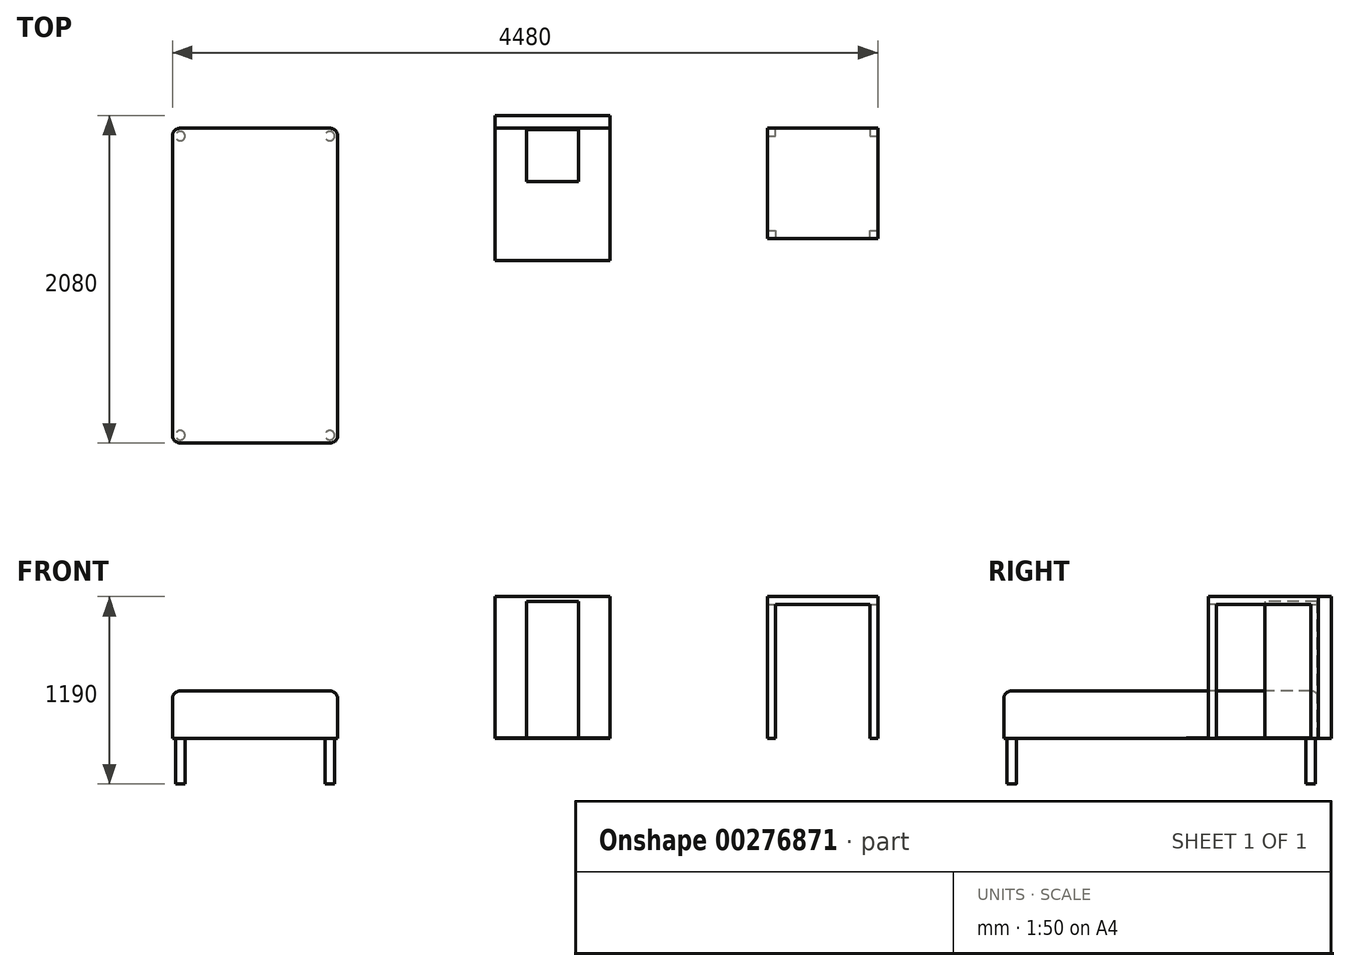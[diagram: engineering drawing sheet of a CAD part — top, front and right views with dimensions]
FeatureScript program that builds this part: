
annotation { "Feature Type Name" : "Feature", "Feature Type Description" : "" }
export const myFeature = defineFeature(function(context is Context, id is Id, definition is map)
    precondition{}
    {
        {
            var Q0;
            Q0=qCreatedBy(makeId("Top.planeOp"),FACE);
            var sketch = newSketch(context, id + "F0", { "sketchPlane" : qUnion([Q0])});
            skLineSegment(sketch, "E0.bottom", {"start": v(-500, 0) * mm, "end": v(-1550, 0) * mm});
            skLineSegment(sketch, "E0.top", {"start": v(-500, -2000) * mm, "end": v(-1550, -2000) * mm});
            skLineSegment(sketch, "E0.left", {"start": v(-500, 0) * mm, "end": v(-500, -2000) * mm});
            skLineSegment(sketch, "E0.right", {"start": v(-1550, 0) * mm, "end": v(-1550, -2000) * mm});
            skCircle(sketch, "E1", {"center": v(-1500, -50) * mm, "radius": 30 * mm});
            skCircle(sketch, "E2", {"center": v(-550, -50) * mm, "radius": 30 * mm});
            skCircle(sketch, "E3", {"center": v(-1500, -1950) * mm, "radius": 30 * mm});
            skCircle(sketch, "E4", {"center": v(-550, -1950) * mm, "radius": 30 * mm});
            skLineSegment(sketch, "E5.bottom", {"start": v(500, 0) * mm, "end": v(1230, 0) * mm});
            skLineSegment(sketch, "E5.top", {"start": v(500, -840) * mm, "end": v(1230, -840) * mm});
            skLineSegment(sketch, "E5.left", {"start": v(500, 0) * mm, "end": v(500, -840) * mm});
            skLineSegment(sketch, "E5.right", {"start": v(1230, 0) * mm, "end": v(1230, -840) * mm});
            skLineSegment(sketch, "E6.bottom", {"start": v(700, -10) * mm, "end": v(1030, -10) * mm});
            skLineSegment(sketch, "E6.top", {"start": v(700, -340) * mm, "end": v(1030, -340) * mm});
            skLineSegment(sketch, "E6.left", {"start": v(700, -10) * mm, "end": v(700, -340) * mm});
            skLineSegment(sketch, "E6.right", {"start": v(1030, -10) * mm, "end": v(1030, -340) * mm});
            skLineSegment(sketch, "E7", {"start": v(500, 0) * mm, "end": v(500, 80) * mm});
            skLineSegment(sketch, "E8", {"start": v(500, 80) * mm, "end": v(1230, 80) * mm});
            skLineSegment(sketch, "E9", {"start": v(1230, 80) * mm, "end": v(1230, 0) * mm});
            skSolve(sketch);
        }
        {
            var Q0;
            Q0=makeQuery(id+"F0.imprint","IMPRINT",FACE,{"disambiguationData":[TD([[makeQuery(id+"F0.imprint","IMPRINT",EDGE,{"derivedFrom":sQuery(id+"F0.wireOp",EDGE,"E0.bottom")}),1.0]])]});
            var Q1;
            Q1=makeQuery(id+"F0.imprint","IMPRINT",FACE,{"disambiguationData":[TD([[makeQuery(id+"F0.imprint","IMPRINT",EDGE,{"derivedFrom":sQuery(id+"F0.wireOp",EDGE,"E1")}),1.0]])]});
            var Q2;
            Q2=makeQuery(id+"F0.imprint","IMPRINT",FACE,{"disambiguationData":[TD([[makeQuery(id+"F0.imprint","IMPRINT",EDGE,{"derivedFrom":sQuery(id+"F0.wireOp",EDGE,"E2")}),1.0]])]});
            var Q3;
            Q3=makeQuery(id+"F0.imprint","IMPRINT",FACE,{"disambiguationData":[TD([[makeQuery(id+"F0.imprint","IMPRINT",EDGE,{"derivedFrom":sQuery(id+"F0.wireOp",EDGE,"E4")}),1.0]])]});
            var Q4;
            Q4=makeQuery(id+"F0.imprint","IMPRINT",FACE,{"disambiguationData":[TD([[makeQuery(id+"F0.imprint","IMPRINT",EDGE,{"derivedFrom":sQuery(id+"F0.wireOp",EDGE,"E3")}),1.0]])]});
            extrude(context, id + "F1", {"entities" : qUnion([Q0, Q1, Q2, Q3, Q4]), "depth" : 300 * mm});
        }
        {
            var Q0;
            Q0=makeQuery(id+"F0.imprint","IMPRINT",FACE,{"disambiguationData":[TD([[makeQuery(id+"F0.imprint","IMPRINT",EDGE,{"derivedFrom":sQuery(id+"F0.wireOp",EDGE,"E2")}),1.0]])]});
            var Q1;
            Q1=makeQuery(id+"F0.imprint","IMPRINT",FACE,{"disambiguationData":[TD([[makeQuery(id+"F0.imprint","IMPRINT",EDGE,{"derivedFrom":sQuery(id+"F0.wireOp",EDGE,"E1")}),1.0]])]});
            var Q2;
            Q2=makeQuery(id+"F0.imprint","IMPRINT",FACE,{"disambiguationData":[TD([[makeQuery(id+"F0.imprint","IMPRINT",EDGE,{"derivedFrom":sQuery(id+"F0.wireOp",EDGE,"E3")}),1.0]])]});
            var Q3;
            Q3=makeQuery(id+"F0.imprint","IMPRINT",FACE,{"disambiguationData":[TD([[makeQuery(id+"F0.imprint","IMPRINT",EDGE,{"derivedFrom":sQuery(id+"F0.wireOp",EDGE,"E4")}),1.0]])]});
            extrude(context, id + "F2", {"entities" : qUnion([Q0, Q1, Q2, Q3]), "operationType" : NewBodyOperationType.ADD, "oppositeDirection" : true, "depth" : 290 * mm});
        }
        {
            var Q0;
            Q0=makeQuery(id+"F1.opExtrude","SWEPT_EDGE",EDGE,{"disambiguationData":[OSD([sQuery(id+"F0.wireOp",EDGE,"E0.bottom"),sQuery(id+"F0.wireOp",EDGE,"E0.right")])]});
            var Q1;
            Q1=makeQuery(id+"F1.opExtrude","SWEPT_EDGE",EDGE,{"disambiguationData":[OSD([sQuery(id+"F0.wireOp",EDGE,"E0.top"),sQuery(id+"F0.wireOp",EDGE,"E0.right")])]});
            var Q2;
            Q2=makeQuery(id+"F1.opExtrude","SWEPT_EDGE",EDGE,{"disambiguationData":[OSD([sQuery(id+"F0.wireOp",EDGE,"E0.top"),sQuery(id+"F0.wireOp",EDGE,"E0.left")])]});
            var Q3;
            Q3=makeQuery(id+"F1.opExtrude","SWEPT_EDGE",EDGE,{"disambiguationData":[OSD([sQuery(id+"F0.wireOp",EDGE,"E0.bottom"),sQuery(id+"F0.wireOp",EDGE,"E0.left")])]});
            var Q4;
            Q4=makeQuery(id+"F1.opExtrude","CAP_FACE",FACE,{"disambiguationData":[OSD([sQuery(id+"F0.wireOp",EDGE,"E0.bottom"),sQuery(id+"F0.wireOp",EDGE,"E0.top"),sQuery(id+"F0.wireOp",EDGE,"E0.left"),sQuery(id+"F0.wireOp",EDGE,"E0.right")])],"isStart":false});
            fillet(context, id + "F3", {"entities" : qUnion([Q0, Q1, Q2, Q3, Q4]), "radius" : 50 * mm, "tangentPropagation" : true, "allowEdgeOverflow" : false});
        }
        {
            var Q0;
            Q0=makeQuery(id+"F0.imprint","IMPRINT",FACE,{"disambiguationData":[TD([[makeQuery(id+"F0.imprint","IMPRINT",EDGE,{"derivedFrom":sQuery(id+"F0.wireOp",EDGE,"E6.bottom")}),-1.0]])]});
            extrude(context, id + "F4", {"entities" : qUnion([Q0]), "depth" : 870 * mm});
        }
        {
            var Q0;
            Q0=makeQuery(id+"F0.imprint","IMPRINT",FACE,{"disambiguationData":[TD([[makeQuery(id+"F0.imprint","IMPRINT",EDGE,{"derivedFrom":sQuery(id+"F0.wireOp",EDGE,"E5.bottom")}),-1.0]])]});
            extrude(context, id + "F5", {"entities" : qUnion([Q0]), "operationType" : NewBodyOperationType.ADD, "depth" : 2 * mm});
        }
        {
            var Q0;
            Q0=makeQuery(id+"F0.imprint","IMPRINT",FACE,{"disambiguationData":[TD([[makeQuery(id+"F0.imprint","IMPRINT",EDGE,{"derivedFrom":sQuery(id+"F0.wireOp",EDGE,"E5.bottom")}),1.0]])]});
            extrude(context, id + "F6", {"entities" : qUnion([Q0]), "operationType" : NewBodyOperationType.ADD, "depth" : 900 * mm});
        }
        {
            var Q0;
            Q0=qCreatedBy(makeId("Top.planeOp"),FACE);
            cPlane(context, id + "F7", {"entities" : qUnion([Q0]), "cplaneType" : CPlaneType.OFFSET, "offset" : 900 * mm, "width" : 150 * mm, "height" : 150 * mm});
        }
        {
            var Q0;
            Q0=qCreatedBy(id+"F7.planeOp",FACE);
            var sketch = newSketch(context, id + "F8", { "sketchPlane" : qUnion([Q0])});
            skLineSegment(sketch, "E10.bottom", {"start": v(2230, 0) * mm, "end": v(2930, 0) * mm});
            skLineSegment(sketch, "E10.top", {"start": v(2230, -700) * mm, "end": v(2930, -700) * mm});
            skLineSegment(sketch, "E10.left", {"start": v(2230, 0) * mm, "end": v(2230, -700) * mm});
            skLineSegment(sketch, "E10.right", {"start": v(2930, 0) * mm, "end": v(2930, -700) * mm});
            skLineSegment(sketch, "E11", {"start": v(2230, -650) * mm, "end": v(2280, -650) * mm});
            skLineSegment(sketch, "E12", {"start": v(2280, -650) * mm, "end": v(2280, -700) * mm});
            skLineSegment(sketch, "E13", {"start": v(2880, 0) * mm, "end": v(2880, -50) * mm});
            skLineSegment(sketch, "E14", {"start": v(2880, -50) * mm, "end": v(2930, -50) * mm});
            skLineSegment(sketch, "E15", {"start": v(2230, -50) * mm, "end": v(2280, -50) * mm});
            skLineSegment(sketch, "E16", {"start": v(2280, -50) * mm, "end": v(2280, 0) * mm});
            skLineSegment(sketch, "E17", {"start": v(2880, -700) * mm, "end": v(2880, -650) * mm});
            skLineSegment(sketch, "E18", {"start": v(2880, -650) * mm, "end": v(2930, -650) * mm});
            skSolve(sketch);
        }
        {
            var Q0;
            {var subQ4=sQuery(id+"F8.wireOp",EDGE,"E11");Q0=makeQuery(id+"F8.imprint","IMPRINT",FACE,{"disambiguationData":[TD([[makeQuery(id+"F8.imprint","IMPRINT",EDGE,{"derivedFrom":subQ4}),1.0]])]});}
            var Q1;
            {var subQ4=sQuery(id+"F8.wireOp",EDGE,"E15");Q1=makeQuery(id+"F8.imprint","IMPRINT",FACE,{"disambiguationData":[TD([[makeQuery(id+"F8.imprint","IMPRINT",EDGE,{"derivedFrom":subQ4}),1.0]])]});}
            var Q2;
            {var subQ3=sQuery(id+"F8.wireOp",EDGE,"E13");Q2=makeQuery(id+"F8.imprint","IMPRINT",FACE,{"disambiguationData":[TD([[makeQuery(id+"F8.imprint","IMPRINT",EDGE,{"derivedFrom":subQ3}),1.0]])]});}
            var Q3;
            {var subQ3=sQuery(id+"F8.wireOp",EDGE,"E17");Q3=makeQuery(id+"F8.imprint","IMPRINT",FACE,{"disambiguationData":[TD([[makeQuery(id+"F8.imprint","IMPRINT",EDGE,{"derivedFrom":subQ3}),-1.0]])]});}
            var Q4;
            {var subQ4=sQuery(id+"F8.wireOp",EDGE,"E11");Q4=makeQuery(id+"F8.imprint","IMPRINT",FACE,{"disambiguationData":[TD([[makeQuery(id+"F8.imprint","IMPRINT",EDGE,{"derivedFrom":subQ4}),-1.0]])]});}
            extrude(context, id + "F9", {"entities" : qUnion([Q0, Q1, Q2, Q3, Q4]), "oppositeDirection" : true, "depth" : 50 * mm});
        }
        {
            var Q0;
            {var subQ4=sQuery(id+"F8.wireOp",EDGE,"E11");Q0=makeQuery(id+"F8.imprint","IMPRINT",FACE,{"disambiguationData":[TD([[makeQuery(id+"F8.imprint","IMPRINT",EDGE,{"derivedFrom":subQ4}),-1.0]])]});}
            var Q1;
            {var subQ3=sQuery(id+"F8.wireOp",EDGE,"E17");Q1=makeQuery(id+"F8.imprint","IMPRINT",FACE,{"disambiguationData":[TD([[makeQuery(id+"F8.imprint","IMPRINT",EDGE,{"derivedFrom":subQ3}),-1.0]])]});}
            var Q2;
            {var subQ4=sQuery(id+"F8.wireOp",EDGE,"E15");Q2=makeQuery(id+"F8.imprint","IMPRINT",FACE,{"disambiguationData":[TD([[makeQuery(id+"F8.imprint","IMPRINT",EDGE,{"derivedFrom":subQ4}),1.0]])]});}
            var Q3;
            {var subQ3=sQuery(id+"F8.wireOp",EDGE,"E13");Q3=makeQuery(id+"F8.imprint","IMPRINT",FACE,{"disambiguationData":[TD([[makeQuery(id+"F8.imprint","IMPRINT",EDGE,{"derivedFrom":subQ3}),1.0]])]});}
            var Q4;
            Q4=qCreatedBy(makeId("Top.planeOp"),FACE);
            extrude(context, id + "F10", {"entities" : qUnion([Q0, Q1, Q2, Q3]), "operationType" : NewBodyOperationType.ADD, "endBound" : BoundingType.UP_TO_SURFACE, "oppositeDirection" : true, "endBoundEntityFace" : qUnion([Q4]), "depth" : 25 * mm});
        }
    });
